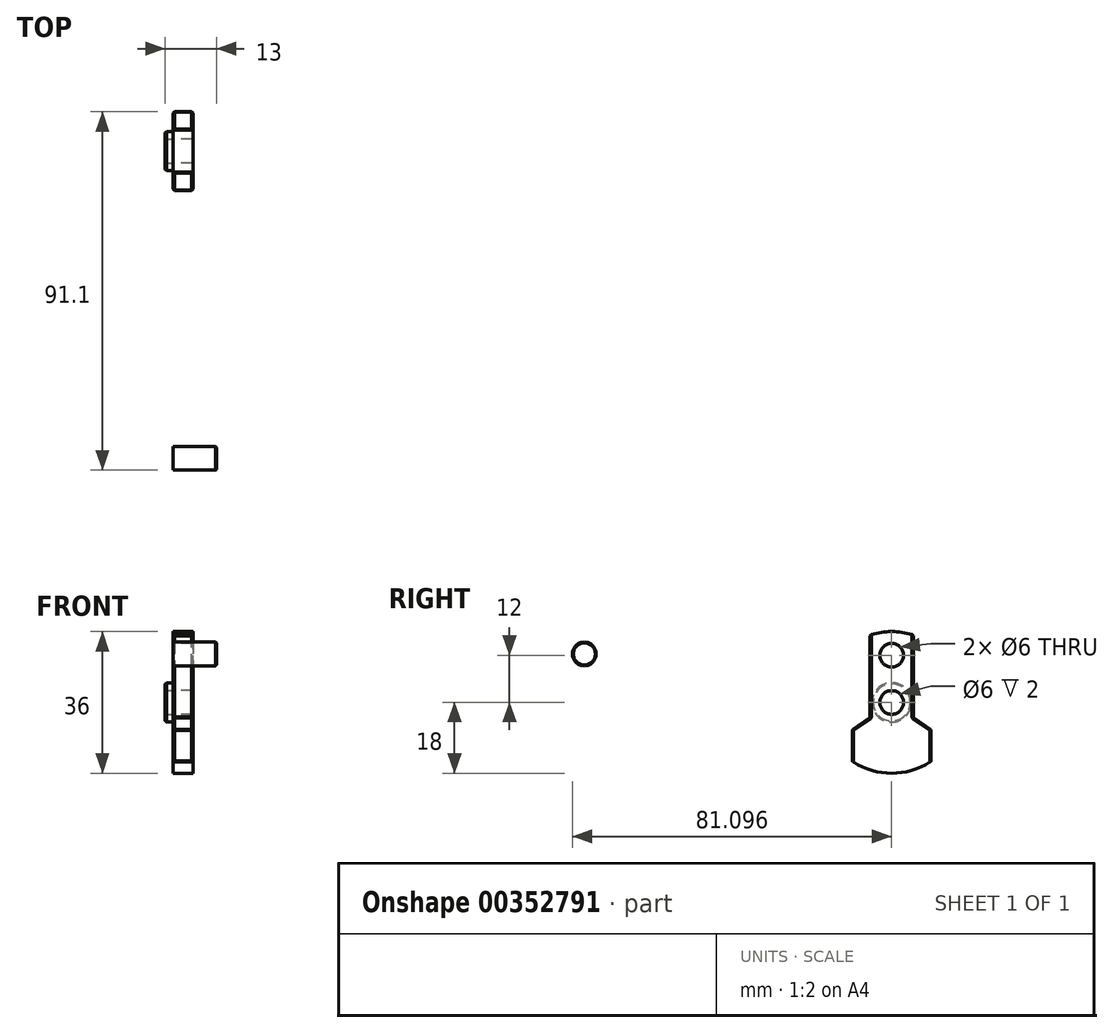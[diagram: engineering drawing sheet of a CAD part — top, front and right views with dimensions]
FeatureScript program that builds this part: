
annotation { "Feature Type Name" : "Feature", "Feature Type Description" : "" }
export const myFeature = defineFeature(function(context is Context, id is Id, definition is map)
    precondition{}
    {
        {
            var Q0;
            Q0=qCreatedBy(makeId("Right.planeOp"),FACE);
            var sketch = newSketch(context, id + "F0", { "sketchPlane" : qUnion([Q0])});
            skCircle(sketch, "E0", {"center": v(28.18, 5) * mm, "radius": 3 * mm});
            skCircle(sketch, "E1", {"center": v(28.18, 17) * mm, "radius": 3 * mm});
            skArc(sketch, "E2", {"start": v(33.68, 22.14) * mm, "mid": v(28.18, 23) * mm, "end": v(22.68, 22.14) * mm});
            skLineSegment(sketch, "E3", {"start": v(18.18, -2) * mm, "end": v(18.18, -9.97) * mm});
            skLineSegment(sketch, "E4.MirrorCS", {"start": v(38.18, -2) * mm, "end": v(38.18, -9.97) * mm});
            skLineSegment(sketch, "E5.MirrorCS", {"start": v(33.68, 22.14) * mm, "end": v(33.68, 1.14) * mm});
            skLineSegment(sketch, "E6.MirrorCS", {"start": v(22.68, 22.14) * mm, "end": v(22.68, 1.14) * mm});
            skArc(sketch, "E7.MirrorC", {"start": v(38.18, -9.97) * mm, "mid": v(28.18, -13) * mm, "end": v(18.18, -9.97) * mm});
            skArc(sketch, "E8.trimOffspring", {"start": v(22.68, 22.14) * mm, "mid": v(28.18, 23) * mm, "end": v(33.68, 22.14) * mm});
            skArc(sketch, "E9.trimOffspring", {"start": v(18.18, -9.97) * mm, "mid": v(28.18, -13) * mm, "end": v(38.18, -9.97) * mm});
            skPoint(sketch, "E10.startSnap0", {"position": v(28.18, -13) * mm});
            skLineSegment(sketch, "E11", {"start": v(22.68, 1.14) * mm, "end": v(18.18, -2) * mm});
            skLineSegment(sketch, "E12", {"start": v(33.68, 1.14) * mm, "end": v(38.18, -2) * mm});
            skCircle(sketch, "E13", {"center": v(28.18, 5) * mm, "radius": 5 * mm});
            skSolve(sketch);
        }
        {
            var Q0;
            Q0=makeQuery(id+"F0.imprint","IMPRINT",FACE,{"disambiguationData":[TD([[makeQuery(id+"F0.imprint","IMPRINT",EDGE,{"derivedFrom":sQuery(id+"F0.wireOp",EDGE,"E0")}),-1.0]])]});
            extrude(context, id + "F1", {"entities" : qUnion([Q0]), "oppositeDirection" : true, "depth" : 2 * mm});
        }
        {
            var Q0;
            Q0=makeQuery(id+"F0.imprint","IMPRINT",FACE,{"disambiguationData":[TD([[makeQuery(id+"F0.imprint","IMPRINT",EDGE,{"derivedFrom":sQuery(id+"F0.wireOp",EDGE,"E1")}),-1.0]])]});
            var Q1;
            Q1=makeQuery(id+"F0.imprint","IMPRINT",FACE,{"disambiguationData":[TD([[makeQuery(id+"F0.imprint","IMPRINT",EDGE,{"derivedFrom":sQuery(id+"F0.wireOp",EDGE,"E0")}),-1.0]])]});
            extrude(context, id + "F2", {"entities" : qUnion([Q0, Q1]), "depth" : 5 * mm});
        }
        {
            var Q0;
            Q0=makeQuery(id+"F2.opExtrude","CAP_EDGE",EDGE,{"disambiguationData":[OSD([sQuery(id+"F0.wireOp",EDGE,"E8.trimOffspring")])],"isStart":true});
            var Q1;
            Q1=makeQuery(id+"F2.opExtrude","CAP_EDGE",EDGE,{"disambiguationData":[OSD([sQuery(id+"F0.wireOp",EDGE,"E9.trimOffspring")])],"isStart":true});
            var Q2;
            Q2=makeQuery(id+"F2.opExtrude","CAP_EDGE",EDGE,{"disambiguationData":[OSD([sQuery(id+"F0.wireOp",EDGE,"E3")])],"isStart":true});
            var Q3;
            Q3=makeQuery(id+"F2.opExtrude","CAP_EDGE",EDGE,{"disambiguationData":[OSD([sQuery(id+"F0.wireOp",EDGE,"E11")])],"isStart":true});
            var Q4;
            Q4=makeQuery(id+"F2.opExtrude","CAP_EDGE",EDGE,{"disambiguationData":[OSD([sQuery(id+"F0.wireOp",EDGE,"E6.MirrorCS")])],"isStart":true});
            var Q5;
            Q5=makeQuery(id+"F1.opExtrude","CAP_EDGE",EDGE,{"disambiguationData":[OSD([sQuery(id+"F0.wireOp",EDGE,"E13")])],"isStart":false});
            var Q6;
            Q6=makeQuery(id+"F2.opExtrude","CAP_EDGE",EDGE,{"disambiguationData":[OSD([sQuery(id+"F0.wireOp",EDGE,"E5.MirrorCS")])],"isStart":true});
            var Q7;
            Q7=makeQuery(id+"F2.opExtrude","CAP_EDGE",EDGE,{"disambiguationData":[OSD([sQuery(id+"F0.wireOp",EDGE,"E12")])],"isStart":true});
            var Q8;
            Q8=makeQuery(id+"F2.opExtrude","CAP_EDGE",EDGE,{"disambiguationData":[OSD([sQuery(id+"F0.wireOp",EDGE,"E4.MirrorCS")])],"isStart":true});
            var Q9;
            Q9=makeQuery(id+"F2.opExtrude","SWEPT_EDGE",EDGE,{"disambiguationData":[OSD([sQuery(id+"F0.wireOp",EDGE,"E3"),sQuery(id+"F0.wireOp",EDGE,"E11")])]});
            var Q10;
            Q10=makeQuery(id+"F2.opExtrude","SWEPT_EDGE",EDGE,{"disambiguationData":[OSD([sQuery(id+"F0.wireOp",EDGE,"E4.MirrorCS"),sQuery(id+"F0.wireOp",EDGE,"E12")])]});
            var Q11;
            Q11=makeQuery(id+"F2.opExtrude","CAP_EDGE",EDGE,{"disambiguationData":[OSD([sQuery(id+"F0.wireOp",EDGE,"E4.MirrorCS")])],"isStart":false});
            var Q12;
            Q12=makeQuery(id+"F2.opExtrude","CAP_EDGE",EDGE,{"disambiguationData":[OSD([sQuery(id+"F0.wireOp",EDGE,"E12")])],"isStart":false});
            var Q13;
            Q13=makeQuery(id+"F2.opExtrude","CAP_EDGE",EDGE,{"disambiguationData":[OSD([sQuery(id+"F0.wireOp",EDGE,"E5.MirrorCS")])],"isStart":false});
            var Q14;
            Q14=makeQuery(id+"F2.opExtrude","CAP_EDGE",EDGE,{"disambiguationData":[OSD([sQuery(id+"F0.wireOp",EDGE,"E8.trimOffspring")])],"isStart":false});
            var Q15;
            Q15=makeQuery(id+"F2.opExtrude","CAP_EDGE",EDGE,{"disambiguationData":[OSD([sQuery(id+"F0.wireOp",EDGE,"E6.MirrorCS")])],"isStart":false});
            var Q16;
            Q16=makeQuery(id+"F2.opExtrude","CAP_EDGE",EDGE,{"disambiguationData":[OSD([sQuery(id+"F0.wireOp",EDGE,"E11")])],"isStart":false});
            var Q17;
            Q17=makeQuery(id+"F2.opExtrude","CAP_EDGE",EDGE,{"disambiguationData":[OSD([sQuery(id+"F0.wireOp",EDGE,"E3")])],"isStart":false});
            var Q18;
            Q18=makeQuery(id+"F2.opExtrude","CAP_EDGE",EDGE,{"disambiguationData":[OSD([sQuery(id+"F0.wireOp",EDGE,"E9.trimOffspring")])],"isStart":false});
            var Q19;
            Q19=makeQuery(id+"F2.opExtrude","SWEPT_EDGE",EDGE,{"disambiguationData":[OSD([sQuery(id+"F0.wireOp",EDGE,"E5.MirrorCS"),sQuery(id+"F0.wireOp",EDGE,"E8.trimOffspring")])]});
            var Q20;
            Q20=makeQuery(id+"F2.opExtrude","SWEPT_EDGE",EDGE,{"disambiguationData":[OSD([sQuery(id+"F0.wireOp",EDGE,"E6.MirrorCS"),sQuery(id+"F0.wireOp",EDGE,"E8.trimOffspring")])]});
            var Q21;
            Q21=makeQuery(id+"F2.opExtrude","SWEPT_EDGE",EDGE,{"disambiguationData":[OSD([sQuery(id+"F0.wireOp",EDGE,"E3"),sQuery(id+"F0.wireOp",EDGE,"E9.trimOffspring")])]});
            var Q22;
            Q22=makeQuery(id+"F2.opExtrude","SWEPT_EDGE",EDGE,{"disambiguationData":[OSD([sQuery(id+"F0.wireOp",EDGE,"E4.MirrorCS"),sQuery(id+"F0.wireOp",EDGE,"E9.trimOffspring")])]});
            chamfer(context, id + "F3", {"entities" : qUnion([Q0, Q1, Q2, Q3, Q4, Q5, Q6, Q7, Q8, Q9, Q10, Q11, Q12, Q13, Q14, Q15, Q16, Q17, Q18, Q19, Q20, Q21, Q22]), "width" : .3 * mm, "tangentPropagation" : true});
        }
        {
            var Q0;
            Q0=qCreatedBy(makeId("Right.planeOp"),FACE);
            var sketch = newSketch(context, id + "F4", { "sketchPlane" : qUnion([Q0])});
            skCircle(sketch, "E14", {"center": v(-49.92, 17.32) * mm, "radius": 3 * mm});
            skSolve(sketch);
        }
        {
            var Q0;
            Q0 = qSketchRegion(id + "F4", true);
            extrude(context, id + "F5", {"entities" : qUnion([Q0]), "depth" : 11 * mm});
        }
        {
            var Q0;
            Q0=makeQuery(id+"F5.opExtrude","CAP_EDGE",EDGE,{"disambiguationData":[OSD([sQuery(id+"F4.wireOp",EDGE,"E14")])],"isStart":false});
            chamfer(context, id + "F6", {"entities" : qUnion([Q0]), "width" : .2 * mm, "tangentPropagation" : true});
        }
    });
